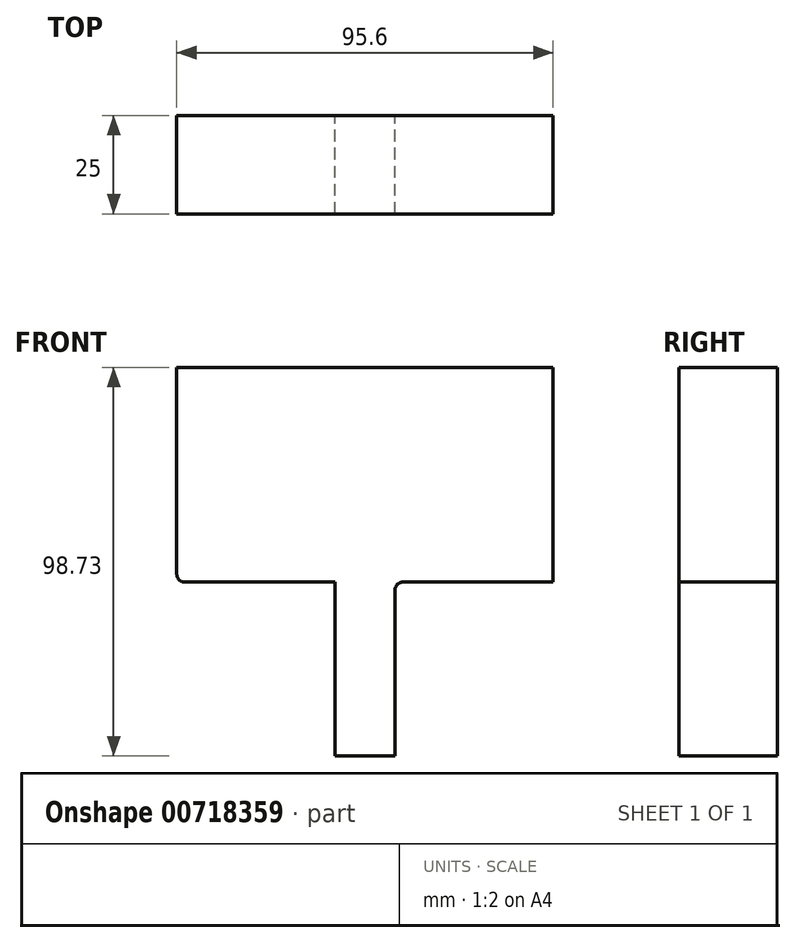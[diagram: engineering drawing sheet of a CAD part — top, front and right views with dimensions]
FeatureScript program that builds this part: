
annotation { "Feature Type Name" : "Feature", "Feature Type Description" : "" }
export const myFeature = defineFeature(function(context is Context, id is Id, definition is map)
    precondition{}
    {
        {
            var Q0;
            Q0=qCreatedBy(makeId("Front.planeOp"),FACE);
            var sketch = newSketch(context, id + "F0", { "sketchPlane" : qUnion([Q0])});
            skLineSegment(sketch, "E0.bottom", {"start": v(47.8, -27.28) * mm, "end": v(9.62, -27.28) * mm});
            skLineSegment(sketch, "E0.top", {"start": v(47.8, 27.28) * mm, "end": v(-47.8, 27.28) * mm});
            skLineSegment(sketch, "E0.left", {"start": v(47.8, -27.28) * mm, "end": v(47.8, 27.28) * mm});
            skLineSegment(sketch, "E0.right", {"start": v(-47.8, -25.28) * mm, "end": v(-47.8, 27.28) * mm});
            skPoint(sketch, "E0.middle", {"position": v(0, 0) * mm});
            skLineSegment(sketch, "E1.top", {"start": v(-7.62, -71.45) * mm, "end": v(7.62, -71.45) * mm});
            skLineSegment(sketch, "E1.left", {"start": v(-7.62, -27.28) * mm, "end": v(-7.62, -71.45) * mm});
            skLineSegment(sketch, "E1.right", {"start": v(7.62, -29.28) * mm, "end": v(7.62, -71.45) * mm});
            skPoint(sketch, "E1.middle", {"position": v(0, -35.72) * mm});
            skPoint(sketch, "E2.orphan", {"position": v(-7.62, 0) * mm});
            skPoint(sketch, "E1.bottom.end.orphan", {"position": v(7.62, 0) * mm});
            skLineSegment(sketch, "E3.trimOffspring", {"start": v(-7.62, -27.28) * mm, "end": v(-45.8, -27.28) * mm});
            skPoint(sketch, "E4.visualSharp", {"position": v(-47.8, -27.28) * mm});
            skArc(sketch, "E4.filletArc", {"start": v(-47.8, -25.28) * mm, "mid": v(-47.21, -26.7) * mm, "end": v(-45.8, -27.28) * mm});
            skPoint(sketch, "E5.visualSharp", {"position": v(7.62, -27.28) * mm});
            skArc(sketch, "E5.filletArc", {"start": v(9.62, -27.28) * mm, "mid": v(8.2, -27.86) * mm, "end": v(7.62, -29.28) * mm});
            skSolve(sketch);
        }
        {
            var Q0;
            Q0=makeQuery(id+"F0.imprint","IMPRINT",FACE,{"disambiguationData":[TD([[makeQuery(id+"F0.imprint","IMPRINT",EDGE,{"derivedFrom":sQuery(id+"F0.wireOp",EDGE,"E0.bottom")}),-1.0]])]});
            extrude(context, id + "F1", {"entities" : qUnion([Q0]), "depth" : 25 * mm, "offsetDistance" : 25 * mm});
        }
    });
